# Revit family: Partition-6and1_Panels_High-Skyfold_Zenith_Premium-12-1_to_14-0_FC_3685_to_4265
name_source: partatom
category: Generic Models
units: mm (PartAtom-declared; Revit-internal decimal feet)

## family parameters
Always vertical = Yes
Can host rebar = No
Cut with Voids When Loaded = No
Host = Ceiling
Maintain Annotation Orientation = No
Part Type = Normal
Room Calculation Point = No
Round Connector Dimension = Use Diameter
Shared = No

## types (1)
- 6 + 1  Panels high
    Beam Height"B" = 15' - 4"
    Beam to Hanger = 0' - 5 9/16"
    Bulkhead Width = 0' - 5 1/4"
    Default Elevation = 0' - 0"
    Description = Custom Powerlift Partitions
    Distance From Acoustic Barrier = 0' - 2"
    Finished Ceiling"A" = 12' - 6 7/8"
    Manufacturer = Skyfold
    Model = Compact Drive System
    Panel Height"F" = 2' - 0 1/4"
    Pocket Width Calc = 5' - 1 7/8"
    Pocket Width"E" = 5' - 1 7/8"
    T.O. Hanger = 14' - 10 7/16"
    Total Panel Height = 12' - 4"
    URL = http://www.skyfold.com
    Wall Thickness = 0' - 11 3/4"

## geometry (parser evidence)
native form markers: Blend x4, Sweep x63
no freeform markers — native parametric forms only
